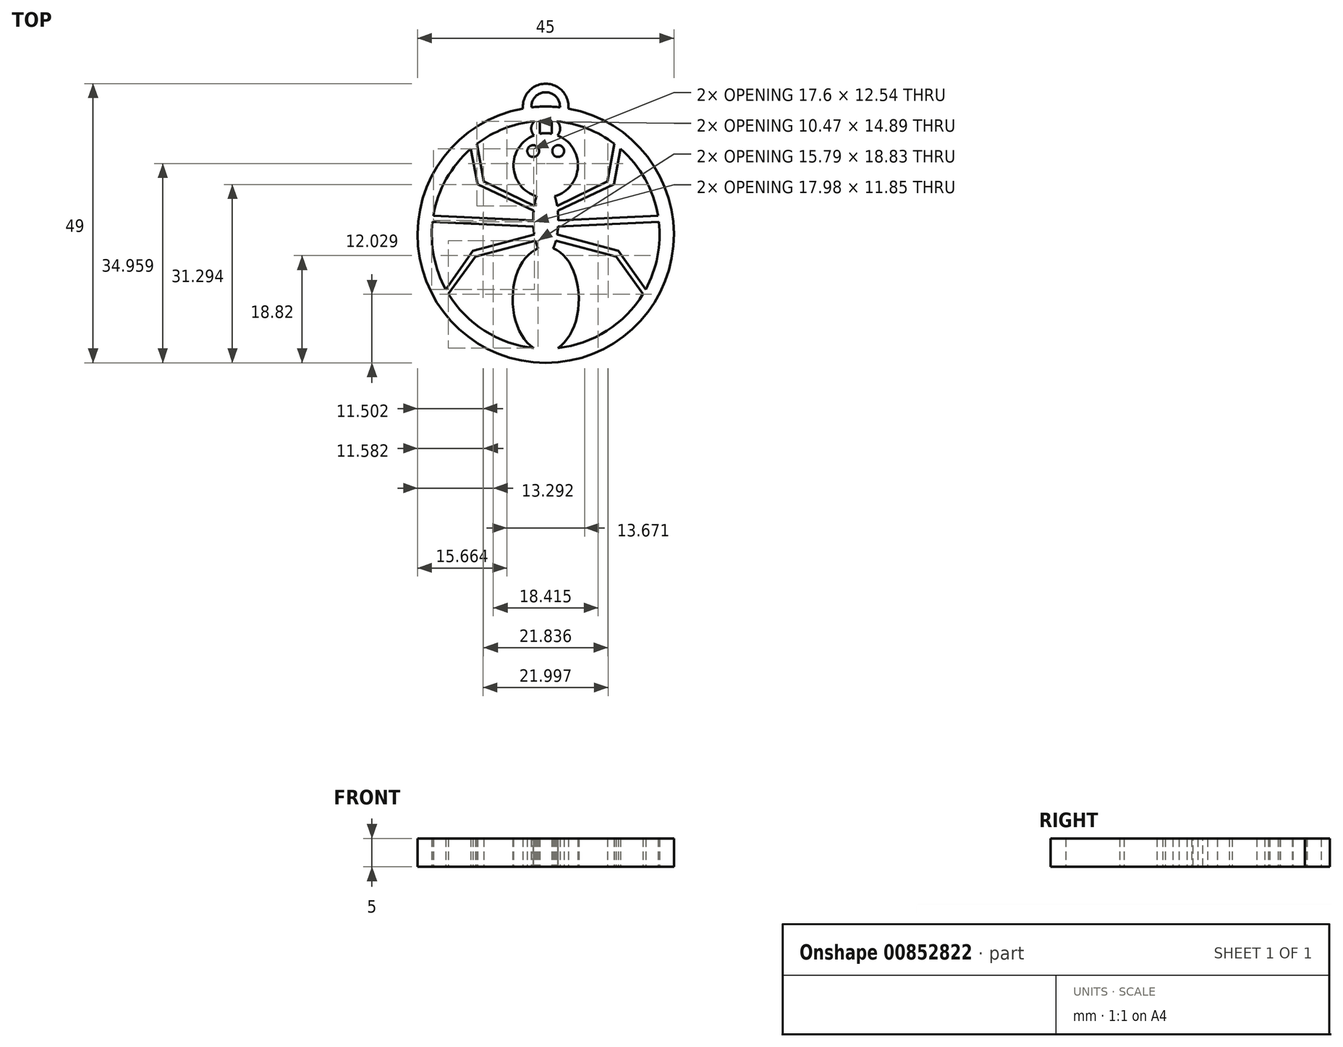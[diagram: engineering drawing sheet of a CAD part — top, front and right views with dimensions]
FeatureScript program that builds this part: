
annotation { "Feature Type Name" : "Feature", "Feature Type Description" : "" }
export const myFeature = defineFeature(function(context is Context, id is Id, definition is map)
    precondition{}
    {
        {
            var Q0;
            Q0=qCreatedBy(makeId("Top.planeOp"),FACE);
            var sketch = newSketch(context, id + "F0", { "sketchPlane" : qUnion([Q0])});
            skArc(sketch, "E0", {"start": v(-1.97, 19.9) * mm, "mid": v(-7.3, 18.62) * mm, "end": v(-12.07, 15.95) * mm});
            skArc(sketch, "E1", {"start": v(2.5, 22.36) * mm, "mid": v(0, 22.5) * mm, "end": v(-2.5, 22.36) * mm});
            skArc(sketch, "E2", {"start": v(1.6, 6.75) * mm, "mid": v(5.65, 11.93) * mm, "end": v(2.06, 17.43) * mm});
            skEllipticalArc(sketch, "E3", {});
            skEllipticalArc(sketch, "E4.trimOffspring", {});
            skLineSegment(sketch, "E5", {"start": v(2.02, 5.02) * mm, "end": v(10.87, 9.35) * mm});
            skLineSegment(sketch, "E6", {"start": v(10.87, 9.35) * mm, "end": v(12.07, 15.95) * mm});
            skLineSegment(sketch, "E7", {"start": v(2.12, 4.22) * mm, "end": v(11.96, 8.85) * mm});
            skLineSegment(sketch, "E8", {"start": v(11.96, 8.85) * mm, "end": v(13.16, 15.06) * mm});
            skLineSegment(sketch, "E9", {"start": v(2.2, 2.53) * mm, "end": v(19.72, 3.35) * mm});
            skLineSegment(sketch, "E10", {"start": v(2.17, 1.4) * mm, "end": v(19.87, 2.24) * mm});
            skLineSegment(sketch, "E11", {"start": v(2, 0) * mm, "end": v(12.75, -2.83) * mm});
            skLineSegment(sketch, "E12", {"start": v(12.75, -2.83) * mm, "end": v(17.54, -9.6) * mm});
            skLineSegment(sketch, "E13", {"start": v(1.8, -1.05) * mm, "end": v(12.36, -3.84) * mm});
            skLineSegment(sketch, "E14", {"start": v(12.36, -3.84) * mm, "end": v(17.1, -10.37) * mm});
            skLineSegment(sketch, "E15.MirrorCS", {"start": v(-2.02, 5.02) * mm, "end": v(-10.87, 9.35) * mm});
            skLineSegment(sketch, "E16.MirrorCS", {"start": v(-10.87, 9.35) * mm, "end": v(-12.07, 15.95) * mm});
            skLineSegment(sketch, "E17.MirrorCS", {"start": v(-11.96, 8.85) * mm, "end": v(-13.16, 15.06) * mm});
            skLineSegment(sketch, "E18.MirrorCS", {"start": v(-2.12, 4.22) * mm, "end": v(-11.96, 8.85) * mm});
            skLineSegment(sketch, "E19.MirrorCS", {"start": v(-2.2, 2.53) * mm, "end": v(-19.72, 3.35) * mm});
            skLineSegment(sketch, "E20.MirrorCS", {"start": v(-2.17, 1.4) * mm, "end": v(-19.87, 2.24) * mm});
            skLineSegment(sketch, "E21.MirrorCS", {"start": v(-2, 0) * mm, "end": v(-12.75, -2.83) * mm});
            skLineSegment(sketch, "E22.MirrorCS", {"start": v(-12.75, -2.83) * mm, "end": v(-17.54, -9.6) * mm});
            skLineSegment(sketch, "E23.MirrorCS", {"start": v(-1.8, -1.05) * mm, "end": v(-12.36, -3.84) * mm});
            skLineSegment(sketch, "E24.MirrorCS", {"start": v(-12.36, -3.84) * mm, "end": v(-17.1, -10.37) * mm});
            skLineSegment(sketch, "E25", {"start": v(1.06, 19.97) * mm, "end": v(1.06, 17.72) * mm});
            skArc(sketch, "E26", {"start": v(2.06, 17.43) * mm, "mid": v(2.54, 18.69) * mm, "end": v(1.97, 19.9) * mm});
            skLineSegment(sketch, "E27.MirrorCS", {"start": v(-1.06, 19.97) * mm, "end": v(-1.06, 17.72) * mm});
            skArc(sketch, "E28.MirrorCS", {"start": v(-2.06, 17.43) * mm, "mid": v(-2.54, 18.69) * mm, "end": v(-1.97, 19.9) * mm});
            skPoint(sketch, "E29.orphan", {"position": v(-1.06, 20.33) * mm});
            skArc(sketch, "E30.trimOffspring", {"start": v(-2.06, 17.43) * mm, "mid": v(-5.65, 11.93) * mm, "end": v(-1.6, 6.75) * mm});
            skPoint(sketch, "E31.orphan", {"position": v(-1.06, 16.92) * mm});
            skPoint(sketch, "E32.orphan", {"position": v(1.06, 16.92) * mm});
            skArc(sketch, "E33.trimOffspring", {"start": v(1.06, 17.72) * mm, "mid": v(0, 17.82) * mm, "end": v(-1.06, 17.72) * mm});
            skArc(sketch, "E34.trimOffspring", {"start": v(1.06, 19.97) * mm, "mid": v(0, 20) * mm, "end": v(-1.06, 19.97) * mm});
            skPoint(sketch, "E35.orphan", {"position": v(1.06, 20.33) * mm});
            skArc(sketch, "E36.trimOffspring", {"start": v(-13.16, 15.06) * mm, "mid": v(-17.45, 9.77) * mm, "end": v(-19.72, 3.35) * mm});
            skArc(sketch, "E37.trimOffspring", {"start": v(12.07, 15.95) * mm, "mid": v(7.3, 18.62) * mm, "end": v(1.97, 19.9) * mm});
            skArc(sketch, "E38.trimOffspring", {"start": v(-19.87, 2.24) * mm, "mid": v(-19.62, -3.86) * mm, "end": v(-17.54, -9.6) * mm});
            skEllipticalArc(sketch, "E39.trimOffspring", {});
            skEllipticalArc(sketch, "E40.trimOffspring", {});
            skEllipticalArc(sketch, "E41.trimOffspring", {});
            skEllipticalArc(sketch, "E42.trimOffspring", {});
            skArc(sketch, "E43.trimOffspring", {"start": v(19.72, 3.35) * mm, "mid": v(17.45, 9.77) * mm, "end": v(13.16, 15.06) * mm});
            skEllipticalArc(sketch, "E44.trimOffspring", {});
            skEllipticalArc(sketch, "E45.trimOffspring", {});
            skArc(sketch, "E46.trimOffspring", {"start": v(-17.1, -10.37) * mm, "mid": v(-10.72, -16.88) * mm, "end": v(-2.11, -19.89) * mm});
            skArc(sketch, "E47.trimOffspring", {"start": v(17.54, -9.6) * mm, "mid": v(19.62, -3.86) * mm, "end": v(19.87, 2.24) * mm});
            skPoint(sketch, "E48.center.orphan", {"position": v(0, -11.34) * mm});
            skEllipticalArc(sketch, "E49", {});
            skEllipticalArc(sketch, "E50.trimOffspring", {});
            skArc(sketch, "E51.trimOffspring", {"start": v(2.11, -19.89) * mm, "mid": v(10.72, -16.88) * mm, "end": v(17.1, -10.37) * mm});
            skCircle(sketch, "E52", {"center": v(2.2, 14.68) * mm, "radius": 1.04 * mm});
            skCircle(sketch, "E53.MirrorC", {"center": v(-2.2, 14.68) * mm, "radius": 1.04 * mm});
            skArc(sketch, "E54", {"start": v(2.5, 22.36) * mm, "mid": v(0, 25) * mm, "end": v(-2.5, 22.36) * mm});
            skArc(sketch, "E55", {"start": v(3.98, 22.14) * mm, "mid": v(0, 26.5) * mm, "end": v(-3.98, 22.14) * mm});
            skArc(sketch, "E56.trimOffspring", {"start": v(-3.98, 22.14) * mm, "mid": v(0, -22.5) * mm, "end": v(3.98, 22.14) * mm});
            const initialGuessF0  = {"E3": [0, 0.002525721676647663, 0, -1, 0.0061449583154171705, 0.0022043163845900716, 3.954994697720543, 4.295144281621939], "E4.trimOffspring": [0, 0.002525721676647663, 0, -1, 0.0061449583154171705, 0.0022043163845900716, 0.6383352558313283, 0.9489920434186496], "E39.trimOffspring": [0, 0.002525721676647663, 0, -1, 0.0061449583154171705, 0.0022043163845900716, 4.432328294756401, 4.71238898038469], "E40.trimOffspring": [0, 0.002525721676647663, 0, -1, 0.0061449583154171705, 0.0022043163845900716, 1.988041025557648, 2.3281906094590434], "E41.trimOffspring": [0, 0.002525721676647663, 0, -1, 0.0061449583154171705, 0.0022043163845900716, 1.5707963267948966, 1.8508570124231858], "E42.trimOffspring": [0, 0.002525721676647663, 0, -1, 0.0061449583154171705, 0.0022043163845900716, 4.895197182675564, 5.135965372854452], "E44.trimOffspring": [0, 0.002525721676647663, 0, -1, 0.0061449583154171705, 0.0022043163845900716, 5.334193263760937, 5.644850051348257], "E45.trimOffspring": [0, 0.002525721676647663, 0, -1, 0.0061449583154171705, 0.0022043163845900716, 1.147219934325134, 1.3879881245040222], "E49": [0, -0.011344538070261478, 0, 1, 0.009173089172691107, 0.005806420949492191, 0.228183642803459, 2.7689132091061808], "E50.trimOffspring": [0, -0.011344538070261478, 0, 1, 0.009173089172691107, 0.005806420949492191, 3.514272098073406, 6.055001664376127]};
            skSetInitialGuess(sketch, initialGuessF0);
            skSolve(sketch);
        }
        {
            var Q0;
            Q0=makeQuery(id+"F0.imprint","IMPRINT",FACE,{"disambiguationData":[TD([[makeQuery(id+"F0.imprint","IMPRINT",EDGE,{"derivedFrom":sQuery(id+"F0.wireOp",EDGE,"E0")}),-1.0]])]});
            extrude(context, id + "F1", {"entities" : qUnion([Q0]), "depth" : 5 * mm, "offsetDistance" : 25 * mm});
        }
    });
